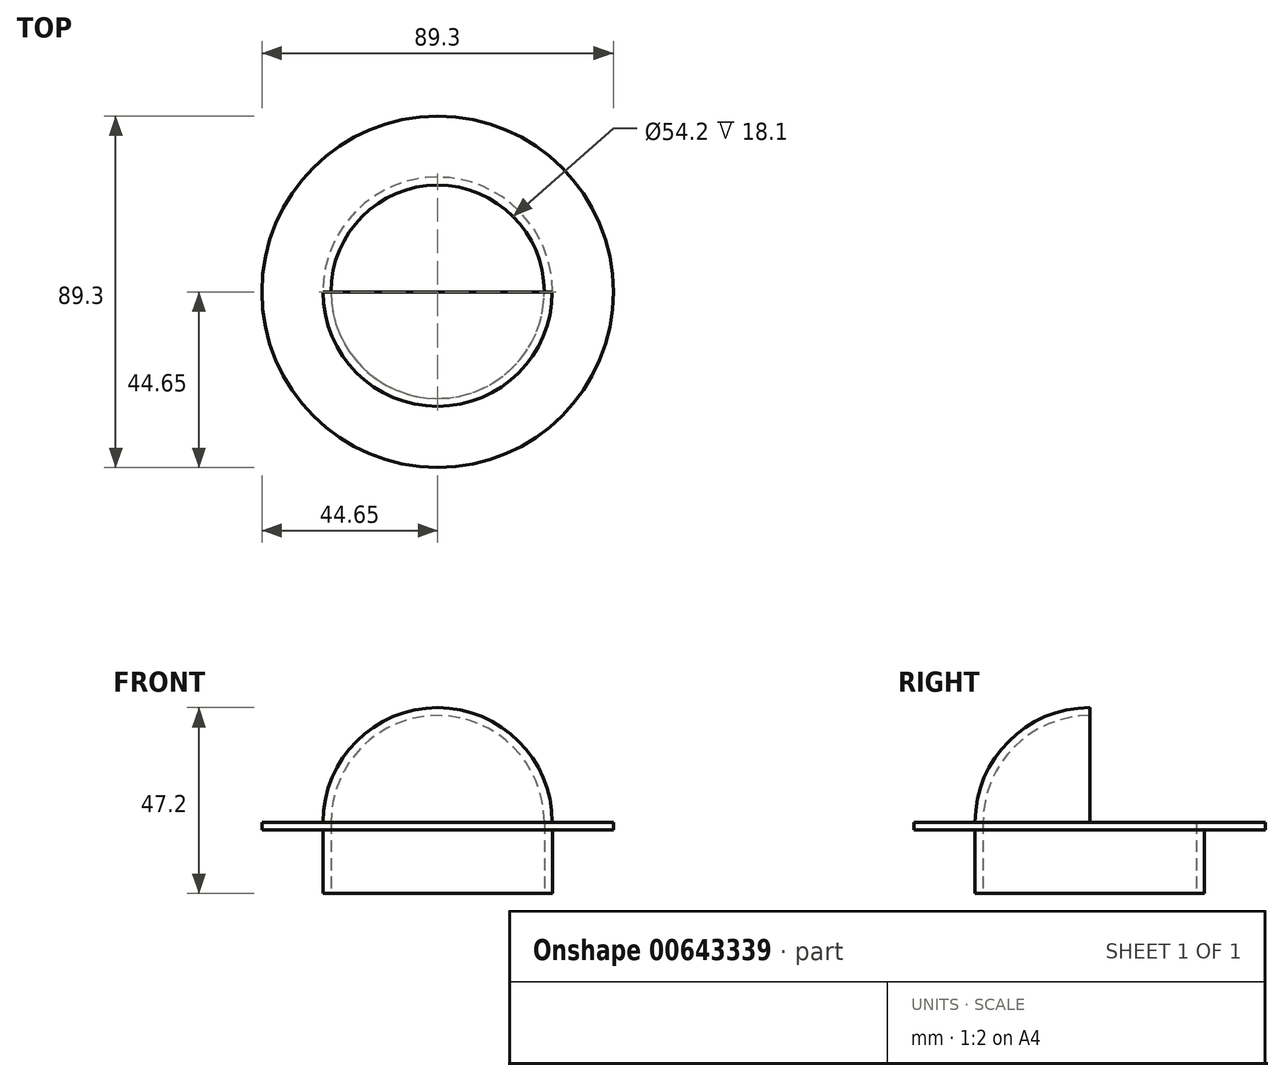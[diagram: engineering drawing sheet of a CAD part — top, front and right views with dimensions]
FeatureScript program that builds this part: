
annotation { "Feature Type Name" : "Feature", "Feature Type Description" : "" }
export const myFeature = defineFeature(function(context is Context, id is Id, definition is map)
    precondition{}
    {
        {
            var Q0;
            Q0=qCreatedBy(makeId("Top.planeOp"),FACE);
            var sketch = newSketch(context, id + "F0", { "sketchPlane" : qUnion([Q0])});
            skCircle(sketch, "E0", {"center": v(0, 0) * mm, "radius": 27.1 * mm});
            skCircle(sketch, "E1", {"center": v(0, 0) * mm, "radius": 44.65 * mm});
            skCircle(sketch, "E2", {"center": v(0, 0) * mm, "radius": 29.1 * mm});
            skSolve(sketch);
        }
        {
            var Q0;
            Q0=makeQuery(id+"F0.imprint","IMPRINT",FACE,{"disambiguationData":[TD([[makeQuery(id+"F0.imprint","IMPRINT",EDGE,{"derivedFrom":sQuery(id+"F0.wireOp",EDGE,"E0")}),-1.0]])]});
            var Q1;
            Q1=makeQuery(id+"F0.imprint","IMPRINT",FACE,{"disambiguationData":[TD([[makeQuery(id+"F0.imprint","IMPRINT",EDGE,{"derivedFrom":sQuery(id+"F0.wireOp",EDGE,"E1")}),1.0]])]});
            extrude(context, id + "F1", {"entities" : qUnion([Q0, Q1]), "depth" : 2 * mm, "offsetDistance" : 25 * mm});
        }
        {
            var Q0;
            Q0=makeQuery(id+"F1.opExtrude","CAP_FACE",FACE,{"disambiguationData":[OSD([sQuery(id+"F0.wireOp",EDGE,"E0"),sQuery(id+"F0.wireOp",EDGE,"E1")])],"isStart":false});
            var sketch = newSketch(context, id + "F2", { "sketchPlane" : qUnion([Q0])});
            skArc(sketch, "E3", {"start": v(-27.1, 0) * mm, "mid": v(-19.16, -19.16) * mm, "end": v(0, -27.1) * mm});
            skLineSegment(sketch, "E4", {"start": v(-27.1, 0) * mm, "end": v(-29.1, 0) * mm});
            skLineSegment(sketch, "E5", {"start": v(0, -27.1) * mm, "end": v(0, -29.1) * mm});
            skArc(sketch, "E6", {"start": v(-29.1, 0) * mm, "mid": v(-20.58, -20.58) * mm, "end": v(0, -29.1) * mm});
            skArc(sketch, "E7", {"start": v(-27.1, 0) * mm, "mid": v(-28.1, 1) * mm, "end": v(-29.1, 0) * mm});
            skSolve(sketch);
        }
        {
            var Q0;
            Q0=qCreatedBy(makeId("Right.planeOp"),FACE);
            var sketch = newSketch(context, id + "F3", { "sketchPlane" : qUnion([Q0])});
            skPoint(sketch, "E8", {"position": v(-27.1, 2) * mm});
            skPoint(sketch, "E9", {"position": v(-29.1, 2) * mm});
            skLineSegment(sketch, "E10", {"start": v(-27.1, 2) * mm, "end": v(-27.1, 4) * mm});
            skLineSegment(sketch, "E11", {"start": v(-29.1, 2) * mm, "end": v(-29.1, 4) * mm});
            skLineSegment(sketch, "E12", {"start": v(-27.1, 4) * mm, "end": v(-29.1, 4) * mm});
            skLineSegment(sketch, "E13", {"start": v(-27.1, 2) * mm, "end": v(-29.1, 2) * mm});
            skSolve(sketch);
        }
        {
            var Q0;
            Q0=makeQuery(id+"F2.imprint","IMPRINT",FACE,{"disambiguationData":[TD([[makeQuery(id+"F2.imprint","IMPRINT",EDGE,{"derivedFrom":sQuery(id+"F2.wireOp",EDGE,"E3")}),-1.0]])]});
            var Q1;
            Q1=sQuery(id+"F3.wireOp",EDGE,"E13");
            revolve(context, id + "F4", {"operationType" : NewBodyOperationType.ADD, "entities" : qUnion([Q0]), "axis" : qUnion([Q1]), "revolveType" : RevolveType.ONE_DIRECTION, "oppositeDirection" : true, "angle" : 180 * degree});
        }
        {
            var Q0;
            Q0=makeQuery(id+"F1.opExtrude","CAP_FACE",FACE,{"disambiguationData":[OSD([sQuery(id+"F0.wireOp",EDGE,"E0"),sQuery(id+"F0.wireOp",EDGE,"E1")])],"isStart":true});
            var sketch = newSketch(context, id + "F5", { "sketchPlane" : qUnion([Q0])});
            skCircle(sketch, "E14", {"center": v(0, 0) * mm, "radius": 29.15 * mm});
            skCircle(sketch, "E15", {"center": v(0, 0) * mm, "radius": 27.1 * mm});
            skSolve(sketch);
        }
        {
            var Q0;
            Q0=makeQuery(id+"F5.imprint","IMPRINT",FACE,{"disambiguationData":[TD([[makeQuery(id+"F5.imprint","IMPRINT",EDGE,{"derivedFrom":sQuery(id+"F5.wireOp",EDGE,"E14")}),1.0]])]});
            extrude(context, id + "F6", {"entities" : qUnion([Q0]), "operationType" : NewBodyOperationType.ADD, "depth" : 16.1 * mm, "offsetDistance" : 25 * mm});
        }
    });
